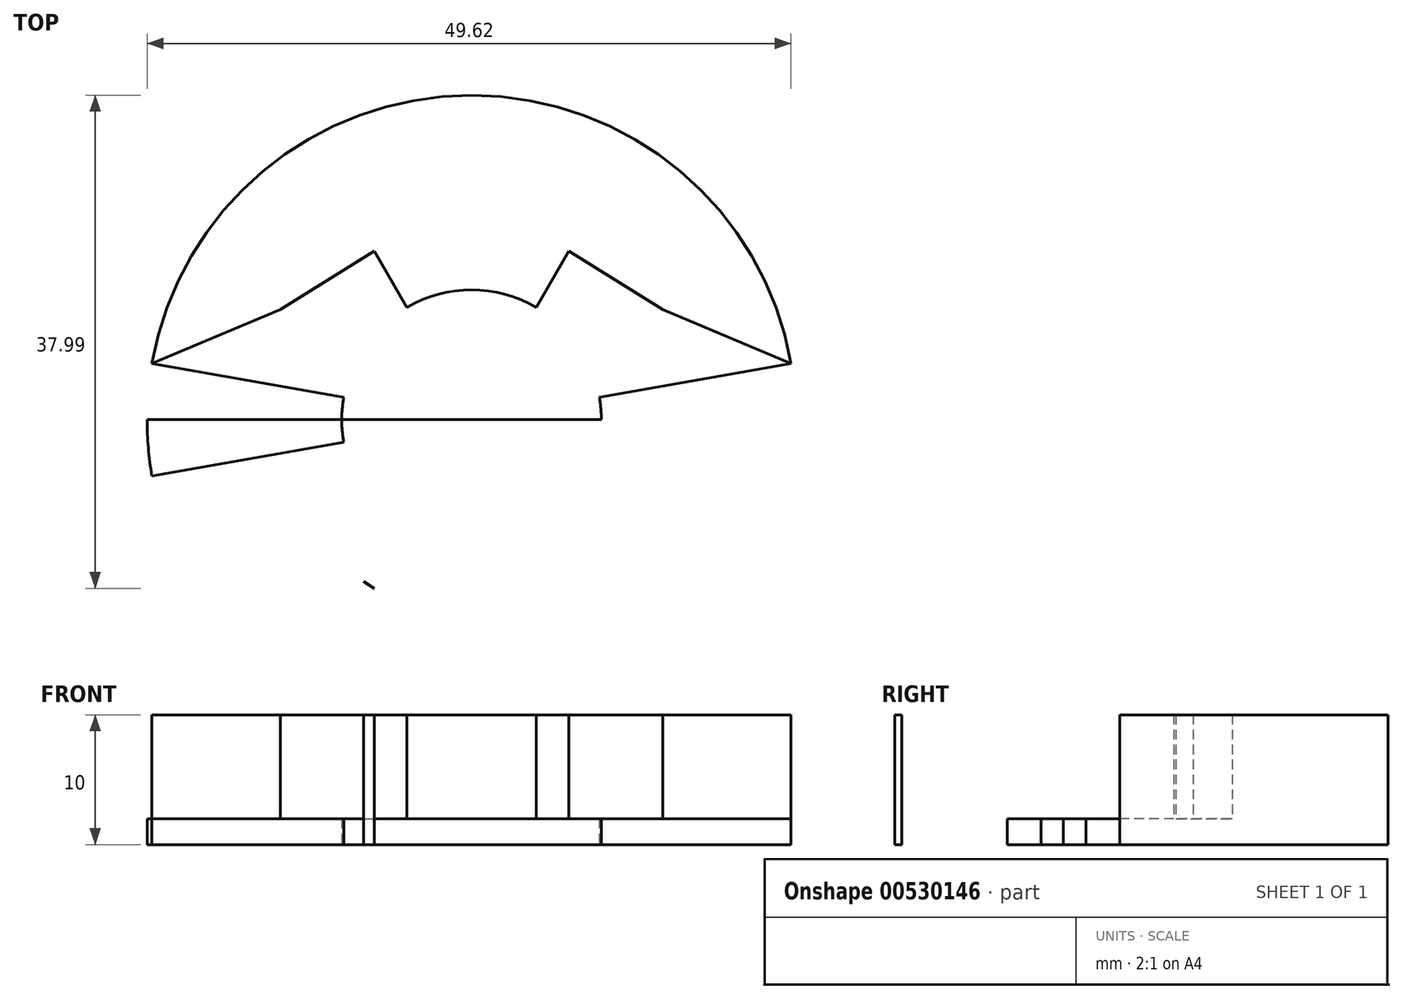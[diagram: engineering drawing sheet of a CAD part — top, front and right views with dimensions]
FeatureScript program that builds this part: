
annotation { "Feature Type Name" : "Feature", "Feature Type Description" : "" }
export const myFeature = defineFeature(function(context is Context, id is Id, definition is map)
    precondition{}
    {
        {
            var Q0;
            Q0=qCreatedBy(makeId("Top.planeOp"),FACE);
            var sketch = newSketch(context, id + "F0", { "sketchPlane" : qUnion([Q0])});
            skArc(sketch, "E0", {"start": v(-9.85, 1.74) * mm, "mid": v(-9.96, 0.87) * mm, "end": v(-10, 0) * mm});
            skLineSegment(sketch, "E1", {"start": v(5, 8.66) * mm, "end": v(7.5, 13) * mm});
            skLineSegment(sketch, "E2.MirrorCS", {"start": v(-5, 8.66) * mm, "end": v(-7.5, 13) * mm});
            skArc(sketch, "E3", {"start": v(25, 0) * mm, "mid": v(0, 25) * mm, "end": v(-25, 0) * mm});
            skLineSegment(sketch, "E4", {"start": v(9.85, 1.74) * mm, "end": v(24.62, 4.34) * mm});
            skLineSegment(sketch, "E5.MirrorCS", {"start": v(-9.85, 1.74) * mm, "end": v(-24.62, 4.34) * mm});
            skLineSegment(sketch, "E6", {"start": v(-7.5, 13) * mm, "end": v(-14.72, 8.5) * mm});
            skLineSegment(sketch, "E7", {"start": v(-14.72, 8.5) * mm, "end": v(-24.62, 4.34) * mm});
            skLineSegment(sketch, "E8", {"start": v(7.5, 13) * mm, "end": v(14.72, 8.5) * mm});
            skLineSegment(sketch, "E9", {"start": v(14.72, 8.5) * mm, "end": v(24.62, 4.34) * mm});
            skArc(sketch, "E10.trimOffspring", {"start": v(5, 8.66) * mm, "mid": v(0, 10) * mm, "end": v(-5, 8.66) * mm});
            skLineSegment(sketch, "E11", {"start": v(-25, 0) * mm, "end": v(25, 0) * mm});
            skArc(sketch, "E12.trimOffspring", {"start": v(10, 0) * mm, "mid": v(9.96, 0.87) * mm, "end": v(9.85, 1.74) * mm});
            skArc(sketch, "E13.MirrorCS", {"start": v(-7.5, -13) * mm, "mid": v(-7.92, -12.74) * mm, "end": v(-8.33, -12.47) * mm});
            skArc(sketch, "E14.MirrorCS", {"start": v(8.33, -12.47) * mm, "mid": v(7.92, -12.74) * mm, "end": v(7.5, -13) * mm});
            skArc(sketch, "E15.MirrorCS", {"start": v(-9.85, -1.74) * mm, "mid": v(-9.96, -0.87) * mm, "end": v(-10, 0) * mm});
            skArc(sketch, "E16.MirrorCS", {"start": v(10, 0) * mm, "mid": v(9.96, -0.87) * mm, "end": v(9.85, -1.74) * mm});
            skLineSegment(sketch, "E17.MirrorCS", {"start": v(-9.85, -1.74) * mm, "end": v(-24.62, -4.34) * mm});
            skArc(sketch, "E18.MirrorCS", {"start": v(25, 0) * mm, "mid": v(0, -25) * mm, "end": v(-25, 0) * mm});
            skLineSegment(sketch, "E19.MirrorCS", {"start": v(-5, -8.66) * mm, "end": v(-7.5, -13) * mm});
            skLineSegment(sketch, "E20.MirrorCS", {"start": v(9.85, -1.74) * mm, "end": v(24.62, -4.34) * mm});
            skLineSegment(sketch, "E21.MirrorCS", {"start": v(5, -8.66) * mm, "end": v(7.5, -13) * mm});
            skLineSegment(sketch, "E22.MirrorCS", {"start": v(-7.5, -13) * mm, "end": v(-14.72, -8.5) * mm});
            skLineSegment(sketch, "E23.MirrorCS", {"start": v(-14.72, -8.5) * mm, "end": v(-24.62, -4.34) * mm});
            skLineSegment(sketch, "E24.MirrorCS", {"start": v(7.5, -13) * mm, "end": v(14.72, -8.5) * mm});
            skLineSegment(sketch, "E25.MirrorCS", {"start": v(14.72, -8.5) * mm, "end": v(24.62, -4.34) * mm});
            skArc(sketch, "E26.MirrorCS", {"start": v(5, -8.66) * mm, "mid": v(0, -10) * mm, "end": v(-5, -8.66) * mm});
            skSolve(sketch);
        }
        {
            var Q0;
            {var subQ1=sQuery(id+"F0.wireOp",EDGE,"E0");Q0=makeQuery(id+"F0.imprint","IMPRINT",FACE,{"disambiguationData":[TD([[makeQuery(id+"F0.imprint","IMPRINT",EDGE,{"derivedFrom":subQ1}),1.0]])]});}
            var Q1;
            {var subQ6=sQuery(id+"F0.wireOp",EDGE,"E15.MirrorCS");Q1=makeQuery(id+"F0.imprint","IMPRINT",FACE,{"disambiguationData":[TD([[makeQuery(id+"F0.imprint","IMPRINT",EDGE,{"derivedFrom":subQ6}),-1.0]])]});}
            extrude(context, id + "F1", {"entities" : qUnion([Q0, Q1]), "depth" : 2 * mm, "offsetDistance" : 25 * mm});
        }
        {
            var Q0;
            Q0=makeQuery(id+"F0.imprint","IMPRINT",FACE,{"disambiguationData":[TD([[makeQuery(id+"F0.imprint","IMPRINT",EDGE,{"derivedFrom":sQuery(id+"F0.wireOp",EDGE,"E1")}),1.0]])]});
            var Q1;
            {var subQ5=sQuery(id+"F0.wireOp",EDGE,"E13.MirrorCS");Q1=makeQuery(id+"F0.imprint","IMPRINT",FACE,{"disambiguationData":[TD([[makeQuery(id+"F0.imprint","IMPRINT",EDGE,{"derivedFrom":subQ5}),1.0]])]});}
            extrude(context, id + "F2", {"entities" : qUnion([Q0, Q1]), "operationType" : NewBodyOperationType.ADD, "depth" : 10 * mm, "offsetDistance" : 25 * mm});
        }
    });
